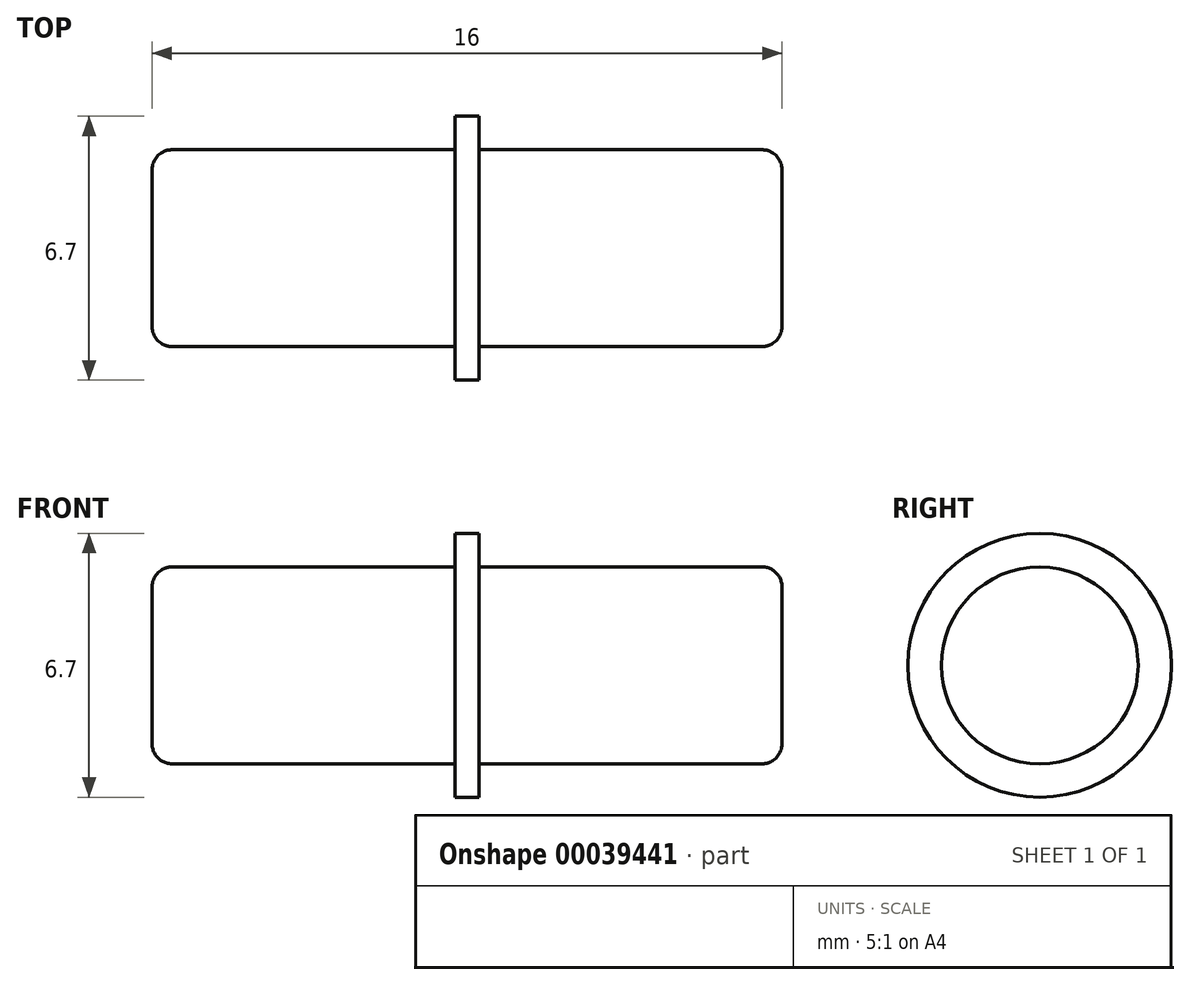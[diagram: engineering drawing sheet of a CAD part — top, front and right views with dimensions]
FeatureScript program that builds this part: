
annotation { "Feature Type Name" : "Feature", "Feature Type Description" : "" }
export const myFeature = defineFeature(function(context is Context, id is Id, definition is map)
    precondition{}
    {
        {
            var Q0;
            Q0=qCreatedBy(makeId("Front.planeOp"),FACE);
            var sketch = newSketch(context, id + "F0", { "sketchPlane" : qUnion([Q0])});
            skLineSegment(sketch, "E0", {"start": v(-8, 0) * mm, "end": v(8, 0) * mm});
            skLineSegment(sketch, "E1", {"start": v(8, 0) * mm, "end": v(8, 2.5) * mm});
            skLineSegment(sketch, "E2", {"start": v(8, 2.5) * mm, "end": v(0.3, 2.5) * mm});
            skLineSegment(sketch, "E3", {"start": v(0.3, 2.5) * mm, "end": v(0.3, 3.35) * mm});
            skLineSegment(sketch, "E4", {"start": v(0.3, 3.35) * mm, "end": v(-0.3, 3.35) * mm});
            skLineSegment(sketch, "E5", {"start": v(-0.3, 3.35) * mm, "end": v(-0.3, 2.5) * mm});
            skLineSegment(sketch, "E6", {"start": v(-0.3, 2.5) * mm, "end": v(-8, 2.5) * mm});
            skLineSegment(sketch, "E7", {"start": v(-8, 2.5) * mm, "end": v(-8, 0) * mm});
            skLineSegment(sketch, "E8", {"start": v(0, 3.35) * mm, "end": v(0, 0) * mm, "construction": true});
            skSolve(sketch);
        }
        {
            var Q0;
            Q0 = qSketchRegion(id + "F0", true);
            var Q1;
            Q1=sQuery(id+"F0.wireOp",EDGE,"E0");
            revolve(context, id + "F1", {"entities" : qUnion([Q0]), "axis" : qUnion([Q1]), "revolveType" : RevolveType.FULL});
        }
        {
            var Q0;
            Q0=makeQuery(id+"F1.opRevolve","SWEPT_EDGE",EDGE,{"disambiguationData":[OSD([sQuery(id+"F0.wireOp",EDGE,"E6"),sQuery(id+"F0.wireOp",EDGE,"E7")])]});
            var Q1;
            Q1=makeQuery(id+"F1.opRevolve","SWEPT_EDGE",EDGE,{"disambiguationData":[OSD([sQuery(id+"F0.wireOp",EDGE,"E1"),sQuery(id+"F0.wireOp",EDGE,"E2")])]});
            fillet(context, id + "F2", {"entities" : qUnion([Q0, Q1]), "radius" : 0.5 * mm, "tangentPropagation" : true, "allowEdgeOverflow" : false});
        }
    });
